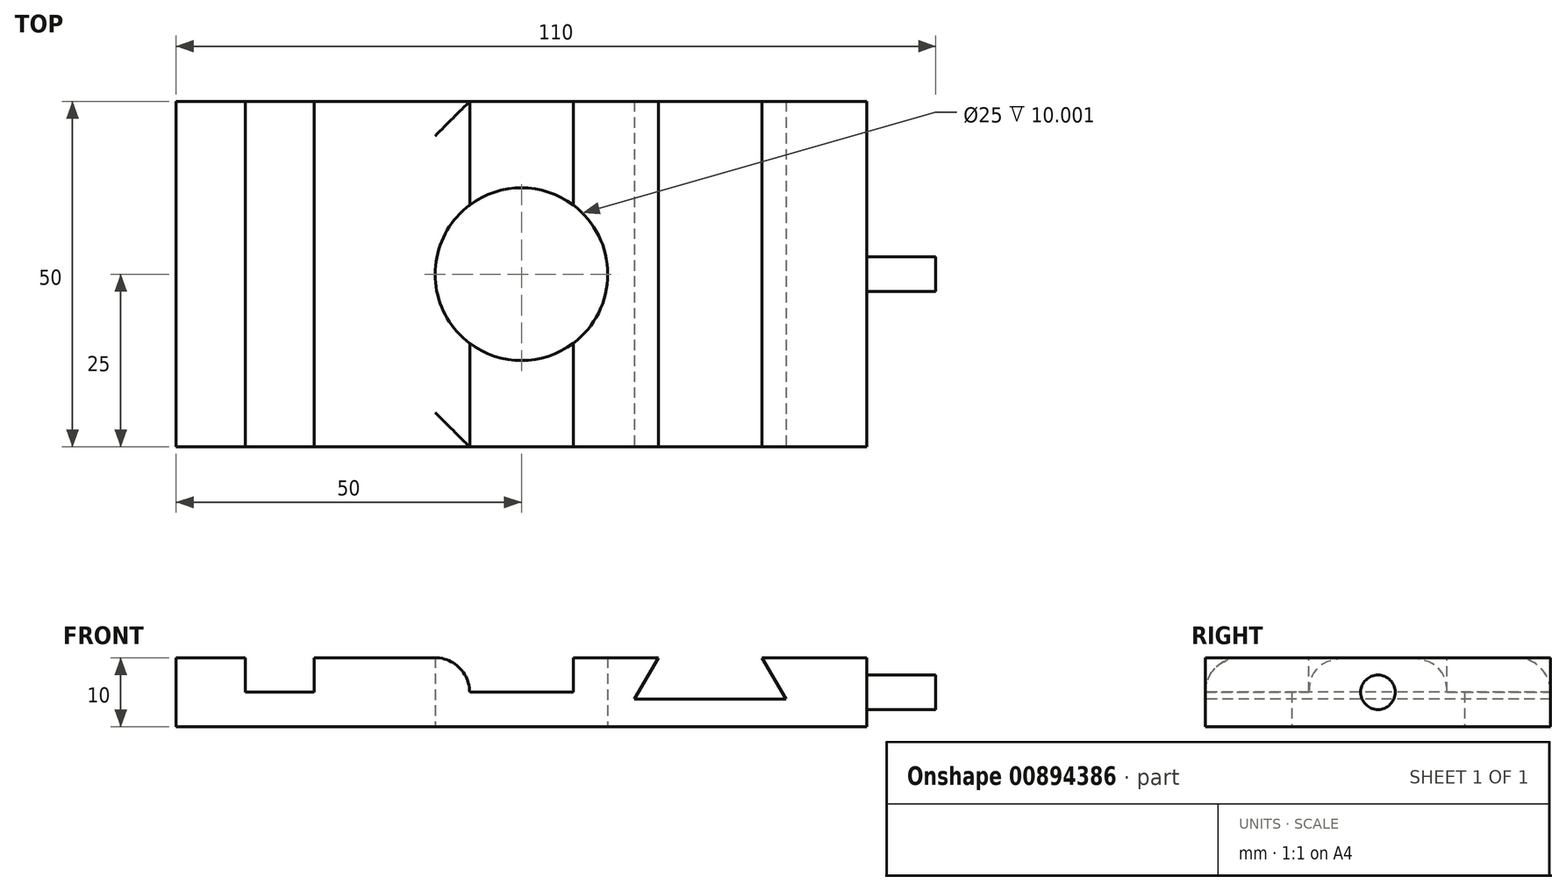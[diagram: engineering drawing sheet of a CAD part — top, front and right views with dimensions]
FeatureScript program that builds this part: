
annotation { "Feature Type Name" : "Feature", "Feature Type Description" : "" }
export const myFeature = defineFeature(function(context is Context, id is Id, definition is map)
    precondition{}
    {
        {
            var Q0;
            Q0=qCreatedBy(makeId("Top.planeOp"),FACE);
            var sketch = newSketch(context, id + "F0", { "sketchPlane" : qUnion([Q0])});
            skLineSegment(sketch, "E0.bottom", {"start": v(-50, 25) * mm, "end": v(50, 25) * mm});
            skLineSegment(sketch, "E0.top", {"start": v(-50, -25) * mm, "end": v(50, -25) * mm});
            skLineSegment(sketch, "E0.left", {"start": v(-50, 25) * mm, "end": v(-50, -25) * mm});
            skLineSegment(sketch, "E0.right", {"start": v(50, 25) * mm, "end": v(50, -25) * mm});
            skPoint(sketch, "E0.middle", {"position": v(0, 0) * mm});
            skCircle(sketch, "E1", {"center": v(0, 0) * mm, "radius": 12.5 * mm});
            skSolve(sketch);
        }
        {
            var Q0;
            Q0=makeQuery(id+"F0.imprint","IMPRINT",FACE,{"disambiguationData":[TD([[makeQuery(id+"F0.imprint","IMPRINT",EDGE,{"derivedFrom":sQuery(id+"F0.wireOp",EDGE,"E0.bottom")}),-1.0]])]});
            extrude(context, id + "F1", {"entities" : qUnion([Q0]), "depth" : 10 * mm, "offsetDistance" : 25.4 * mm});
        }
        {
            var Q0;
            Q0=makeQuery(id+"F1.opExtrude","CAP_FACE",FACE,{"disambiguationData":[OSD([sQuery(id+"F0.wireOp",EDGE,"E0.bottom"),sQuery(id+"F0.wireOp",EDGE,"E0.top"),sQuery(id+"F0.wireOp",EDGE,"E0.left"),sQuery(id+"F0.wireOp",EDGE,"E0.right"),sQuery(id+"F0.wireOp",EDGE,"E1")])],"isStart":false});
            var sketch = newSketch(context, id + "F2", { "sketchPlane" : qUnion([Q0])});
            skLineSegment(sketch, "E2.bottom", {"start": v(-40, 25) * mm, "end": v(-30, 25) * mm});
            skLineSegment(sketch, "E2.top", {"start": v(-40, -25) * mm, "end": v(-30, -25) * mm});
            skLineSegment(sketch, "E2.left", {"start": v(-40, 25) * mm, "end": v(-40, -25) * mm});
            skLineSegment(sketch, "E2.right", {"start": v(-30, 25) * mm, "end": v(-30, -25) * mm});
            skLineSegment(sketch, "E3", {"start": v(-7.5, 25) * mm, "end": v(-7.5, -25) * mm});
            skLineSegment(sketch, "E4", {"start": v(7.5, -25) * mm, "end": v(7.5, 25) * mm});
            skLineSegment(sketch, "E5", {"start": v(7.5, -25) * mm, "end": v(-7.5, -25) * mm});
            skLineSegment(sketch, "E6", {"start": v(7.5, 25) * mm, "end": v(-7.5, 25) * mm});
            skPoint(sketch, "E7", {"position": v(0, 0) * mm});
            skLineSegment(sketch, "E8", {"start": v(0, -25) * mm, "end": v(0, 25) * mm, "construction": true});
            skSolve(sketch);
        }
        {
            var Q0;
            Q0=makeQuery(id+"F2.imprint","IMPRINT",FACE,{"disambiguationData":[TD([[makeQuery(id+"F2.imprint","IMPRINT",EDGE,{"derivedFrom":sQuery(id+"F2.wireOp",EDGE,"E2.bottom")}),-1.0]])]});
            var Q1;
            {var subQ0=sQuery(id+"F2.wireOp",EDGE,"E5");Q1=makeQuery(id+"F2.imprint","IMPRINT",FACE,{"disambiguationData":[TD([[makeQuery(id+"F2.imprint","IMPRINT",EDGE,{"derivedFrom":subQ0}),1.0]])]});}
            var Q2;
            {var subQ0=sQuery(id+"F2.wireOp",EDGE,"E6");Q2=makeQuery(id+"F2.imprint","IMPRINT",FACE,{"disambiguationData":[TD([[makeQuery(id+"F2.imprint","IMPRINT",EDGE,{"derivedFrom":subQ0}),-1.0]])]});}
            extrude(context, id + "F3", {"entities" : qUnion([Q0, Q1, Q2]), "operationType" : NewBodyOperationType.REMOVE, "oppositeDirection" : true, "depth" : 5 * mm, "offsetDistance" : 25 * mm});
        }
        {
            var Q0;
            Q0=makeQuery(id+"F1.opExtrude","SWEPT_FACE",FACE,{"disambiguationData":[OSD([sQuery(id+"F0.wireOp",EDGE,"E0.top")])]});
            var sketch = newSketch(context, id + "F4", { "sketchPlane" : qUnion([Q0])});
            skLineSegment(sketch, "E9", {"start": v(19.83, 10) * mm, "end": v(16.36, 4) * mm});
            skLineSegment(sketch, "E10", {"start": v(16.36, 4) * mm, "end": v(38.3, 4) * mm});
            skLineSegment(sketch, "E11", {"start": v(38.3, 4) * mm, "end": v(34.83, 10) * mm});
            skLineSegment(sketch, "E12", {"start": v(34.83, 10) * mm, "end": v(19.83, 10) * mm});
            skLineSegment(sketch, "E13", {"start": v(27.33, 4) * mm, "end": v(27.33, 10) * mm, "construction": true});
            skSolve(sketch);
        }
        {
            var Q0;
            Q0=makeQuery(id+"F4.imprint","IMPRINT",FACE,{"disambiguationData":[TD([[makeQuery(id+"F4.imprint","IMPRINT",EDGE,{"derivedFrom":sQuery(id+"F4.wireOp",EDGE,"E9")}),1.0]])]});
            extrude(context, id + "F5", {"entities" : qUnion([Q0]), "operationType" : NewBodyOperationType.REMOVE, "endBound" : BoundingType.THROUGH_ALL, "oppositeDirection" : true, "depth" : 25 * mm, "offsetDistance" : 25 * mm});
        }
        {
            var Q0;
            Q0=makeQuery(id+"F1.opExtrude","SWEPT_FACE",FACE,{"disambiguationData":[OSD([sQuery(id+"F0.wireOp",EDGE,"E0.right")])]});
            var sketch = newSketch(context, id + "F6", { "sketchPlane" : qUnion([Q0])});
            skCircle(sketch, "E14", {"center": v(0, 5) * mm, "radius": 2.5 * mm});
            skPoint(sketch, "E14.centerSnap0", {"position": v(-25, 5) * mm});
            skPoint(sketch, "E14.centerSnap1", {"position": v(0, 10) * mm});
            skSolve(sketch);
        }
        {
            var Q0;
            Q0=makeQuery(id+"F6.imprint","IMPRINT",FACE,{"disambiguationData":[TD([[makeQuery(id+"F6.imprint","IMPRINT",EDGE,{"derivedFrom":sQuery(id+"F6.wireOp",EDGE,"E14")}),1.0]])]});
            extrude(context, id + "F7", {"entities" : qUnion([Q0]), "operationType" : NewBodyOperationType.ADD, "depth" : 10 * mm, "offsetDistance" : 25 * mm});
        }
        {
            var Q0;
            {var subQ1=sQuery(id+"F0.wireOp",EDGE,"E0.top");var subQ3=makeQuery(id+"F1.opExtrude","CAP_EDGE",EDGE,{"disambiguationData":[OSD([subQ1])],"isStart":false});Q0=makeQuery(id+"F3.boolean.opBoolean","SPLIT",EDGE,{"disambiguationData":[TD([makeQuery(id+"F3.opExtrude","SWEPT_FACE",FACE,{"disambiguationData":[OSD([sQuery(id+"F2.wireOp",EDGE,"E2.right")])]})])],"derivedFrom":subQ3});}
            var Q1;
            {var subQ0=sQuery(id+"F0.wireOp",EDGE,"E0.bottom");var subQ2=makeQuery(id+"F1.opExtrude","CAP_EDGE",EDGE,{"disambiguationData":[OSD([subQ0])],"isStart":false});Q1=makeQuery(id+"F3.boolean.opBoolean","SPLIT",EDGE,{"disambiguationData":[TD([makeQuery(id+"F3.opExtrude","SWEPT_FACE",FACE,{"disambiguationData":[OSD([sQuery(id+"F2.wireOp",EDGE,"E2.right")])]})])],"derivedFrom":subQ2});}
            var Q2;
            {var subQ0=sQuery(id+"F2.wireOp",EDGE,"E3");Q2=makeQuery(id+"F3.boolean.opBoolean","COPY",EDGE,{"derivedFrom":makeQuery(id+"F3.opExtrude","CAP_EDGE",EDGE,{"disambiguationData":[OSD([subQ0]),TDD([makeQuery(id+"F2.imprint","IMPRINT",EDGE,{"disambiguationData":[TD([[makeQuery(id+"F2.imprint","INTERSECT",VERTEX,{"disambiguationData":[OD(1.0)],"derivedFrom":[makeQuery(id+"F1.opExtrude","CAP_EDGE",EDGE,{"disambiguationData":[OSD([sQuery(id+"F0.wireOp",EDGE,"E1")])],"isStart":false}),subQ0]}),-1.0]])],"derivedFrom":subQ0})])],"isStart":true})});}
            var Q3;
            {var subQ0=sQuery(id+"F2.wireOp",EDGE,"E3");Q3=makeQuery(id+"F3.boolean.opBoolean","COPY",EDGE,{"derivedFrom":makeQuery(id+"F3.opExtrude","CAP_EDGE",EDGE,{"disambiguationData":[OSD([subQ0]),TDD([makeQuery(id+"F2.imprint","IMPRINT",EDGE,{"disambiguationData":[TD([[makeQuery(id+"F2.imprint","INTERSECT",VERTEX,{"disambiguationData":[OD(0.0)],"derivedFrom":[makeQuery(id+"F1.opExtrude","CAP_EDGE",EDGE,{"disambiguationData":[OSD([sQuery(id+"F0.wireOp",EDGE,"E1")])],"isStart":false}),subQ0]}),1.0]])],"derivedFrom":subQ0})])],"isStart":true})});}
            fillet(context, id + "F8", {"entities" : qUnion([Q0, Q1, Q2, Q3]), "radius" : 5 * mm, "tangentPropagation" : true, "allowEdgeOverflow" : false});
        }
    });
